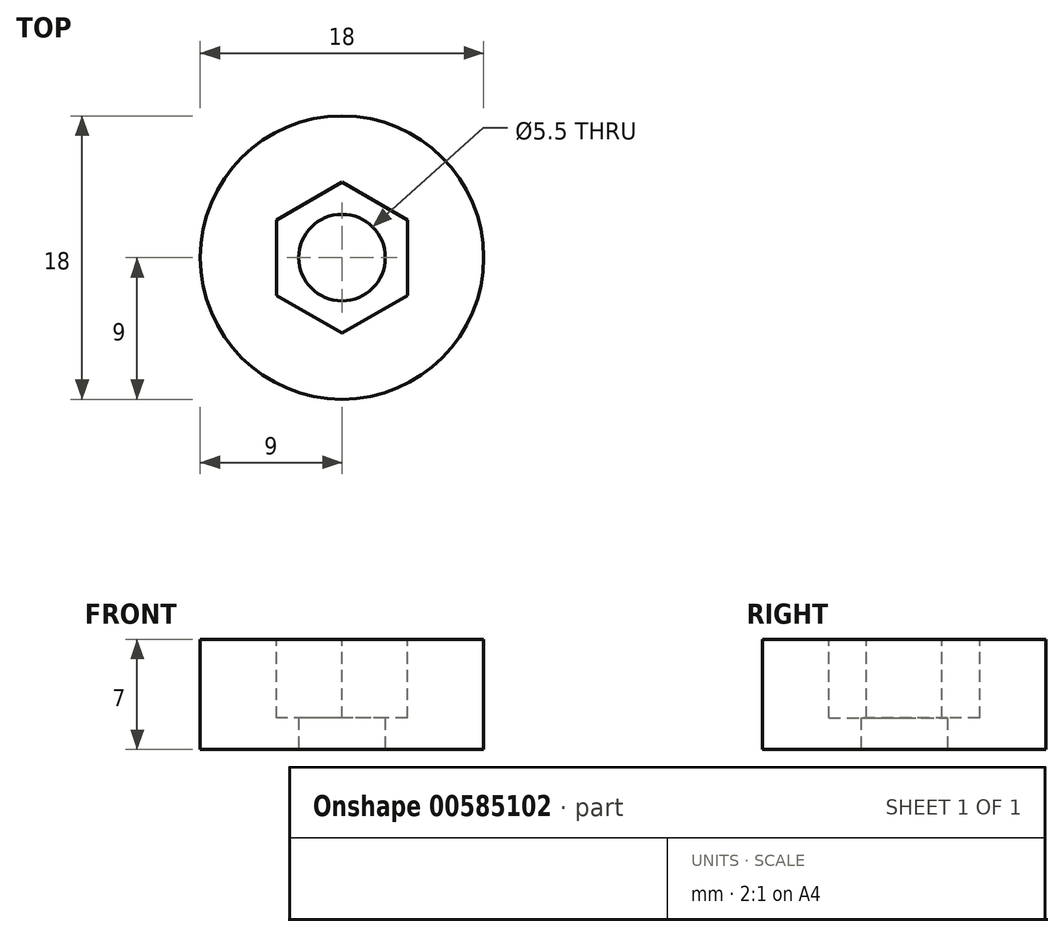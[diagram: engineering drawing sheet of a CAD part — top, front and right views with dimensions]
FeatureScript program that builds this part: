
annotation { "Feature Type Name" : "Feature", "Feature Type Description" : "" }
export const myFeature = defineFeature(function(context is Context, id is Id, definition is map)
    precondition{}
    {
        {
            var Q0;
            Q0=qCreatedBy(makeId("Top.planeOp"),FACE);
            var sketch = newSketch(context, id + "F0", { "sketchPlane" : qUnion([Q0])});
            skCircle(sketch, "E0", {"center": v(0, 0) * mm, "radius": 9 * mm});
            skCircle(sketch, "E1", {"center": v(0, 0) * mm, "radius": 2.75 * mm});
            skSolve(sketch);
        }
        {
            var Q0;
            Q0 = qSketchRegion(id + "F0", true);
            extrude(context, id + "F1", {"entities" : qUnion([Q0]), "depth" : 7 * mm, "offsetDistance" : 25 * mm});
        }
        {
            var Q0;
            Q0=makeQuery(id+"F1.opExtrude","CAP_FACE",FACE,{"disambiguationData":[OSD([sQuery(id+"F0.wireOp",EDGE,"E0"),sQuery(id+"F0.wireOp",EDGE,"E1")])],"isStart":false});
            var sketch = newSketch(context, id + "F2", { "sketchPlane" : qUnion([Q0])});
            skCircle(sketch, "E2.cCircle", {"center": v(0, 0) * mm, "radius": 4.15 * mm, "construction": true});
            skLineSegment(sketch, "E2.0", {"start": v(-4.15, -2.4) * mm, "end": v(-4.15, 2.4) * mm});
            skLineSegment(sketch, "E2.1", {"start": v(-4.15, 2.4) * mm, "end": v(0, 4.8) * mm});
            skLineSegment(sketch, "E2.2", {"start": v(0, 4.8) * mm, "end": v(4.15, 2.4) * mm});
            skLineSegment(sketch, "E2.3", {"start": v(4.15, 2.4) * mm, "end": v(4.15, -2.4) * mm});
            skLineSegment(sketch, "E2.4", {"start": v(4.15, -2.4) * mm, "end": v(0, -4.8) * mm});
            skLineSegment(sketch, "E2.5", {"start": v(0, -4.8) * mm, "end": v(-4.15, -2.4) * mm});
            skPoint(sketch, "E2.0.midPoint", {"position": v(-4.15, 0) * mm});
            skSolve(sketch);
        }
        {
            var Q0;
            Q0 = qSketchRegion(id + "F2", true);
            extrude(context, id + "F3", {"entities" : qUnion([Q0]), "operationType" : NewBodyOperationType.REMOVE, "oppositeDirection" : true, "depth" : 5 * mm, "offsetDistance" : 25 * mm});
        }
    });
